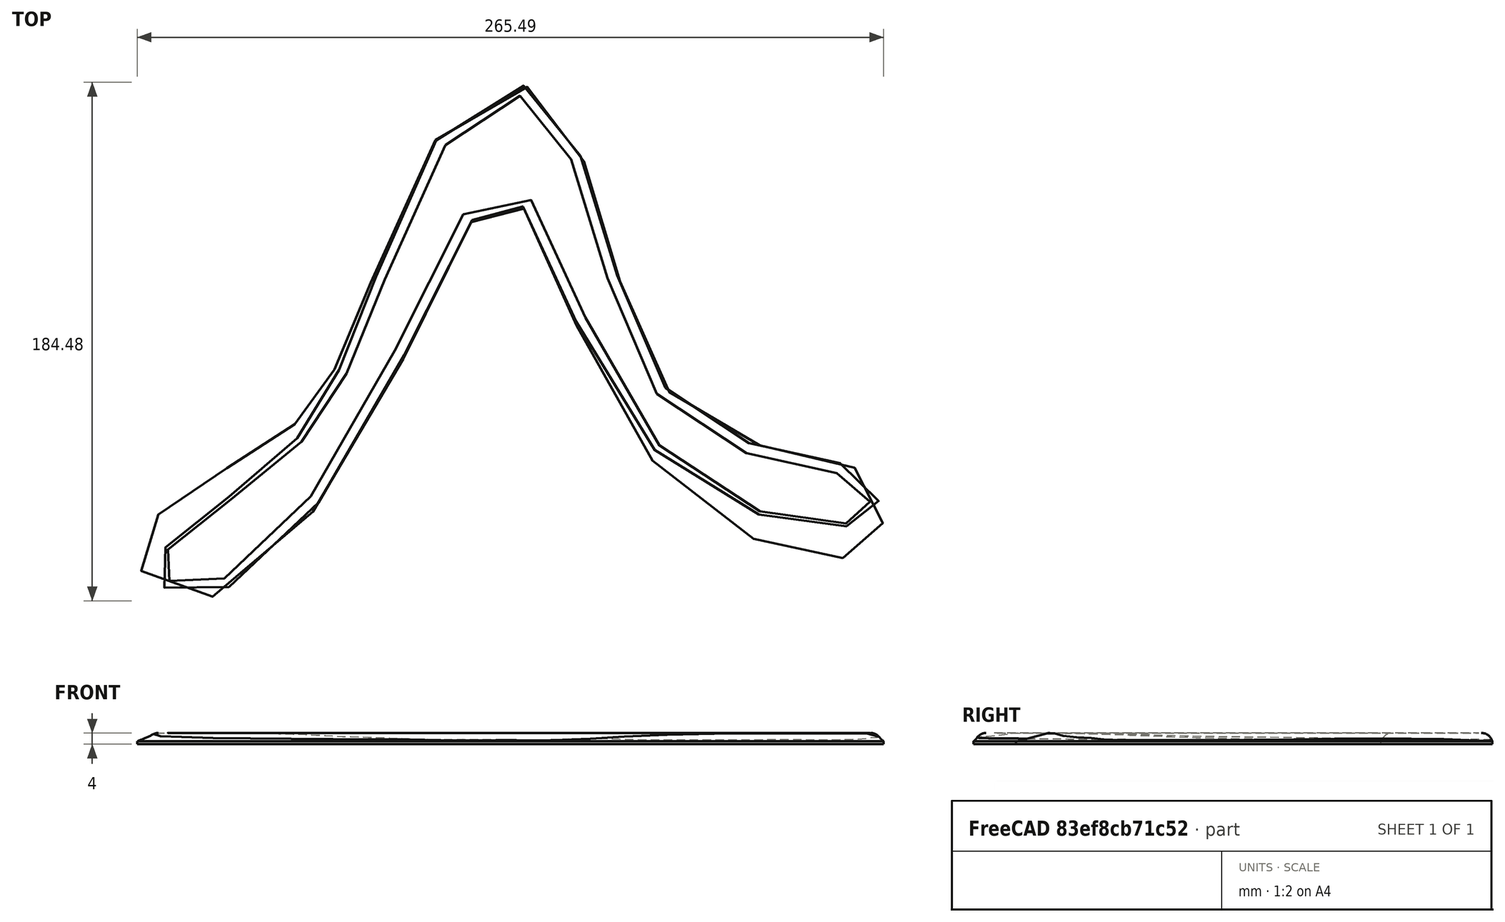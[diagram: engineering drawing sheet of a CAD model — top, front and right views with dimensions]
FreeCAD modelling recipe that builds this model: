
FCSTD DOCUMENT  (FreeCAD 1.2R46491 (Git))
Label: dings
License: All rights reserved
objects: App::Point×2, Sketcher::SketchObject×2, PartDesign::AdditiveLoft×1, PartDesign::Pad×1, PartDesign::Fillet×1, PartDesign::Body×1, App::Part×1
note: 14 computed .brp shape members not serialized (recipe doc carries the construction recipe); baked Part::Feature solids carry a one-line shape summary decoded from their .brp

FEATURE [App::Point] Origin001  label="Origin-Point"
  Role = Origin
FEATURE [App::Point] Origin003  label="Origin-Point001"
  Role = Origin
FEATURE [Sketcher::SketchObject] Sketch  label="Outline"
  ArcFitTolerance = 1e-06
  AttachmentSupport = -> [Origin002]
  ExternalTypes = [0]
  FullyConstrained = false
  MakeInternals = true
  MapMode = 5
  sketch-geometry (29):
    g0: BSplineCurve PolesCount=14 KnotsCount=14 Degree=3 IsPeriodic=1
    g1-g13: GeomPoint [constr] x13 (B-spline internal-alignment scaffolding for g0; pole/knot coordinates omitted)
    g14-g27: Circle [constr] x14 (B-spline internal-alignment scaffolding for g0; pole/knot coordinates omitted)
    g28: GeomPoint [constr] X=-23.3118 Y=8.01846 Z=0
  constraints (29):
    c: InternalAlignment(g1-g14 -> g0) x14
    c: Weight(g14) = 1
    c: InternalAlignment(g15,g0)
    c: Equal(g15,g14)
    c: InternalAlignment(g16,g0)
    c: Equal(g16,g14)
    c: InternalAlignment(g17,g0)
    c: Equal(g17,g14)
    c: InternalAlignment(g18,g0)
    c: Equal(g18,g14)
    c: InternalAlignment(g19,g0)
    c: Equal(g19,g14)
    c: InternalAlignment(g20,g0)
    c: Equal(g20,g14)
    c: InternalAlignment(g21,g0)
    c: Equal(g21,g14)
    c: InternalAlignment(g22,g0)
    c: Equal(g22,g14)
    c: InternalAlignment(g23,g0)
    c: Equal(g23,g14)
    c: InternalAlignment(g24,g0)
    c: Equal(g24,g14)
    c: InternalAlignment(g25,g0)
    c: Equal(g25,g14)
    c: InternalAlignment(g26,g0)
    c: Equal(g26,g14)
    c: InternalAlignment(g27,g0)
    c: Equal(g27,g14)
    c: InternalAlignment(g28,g0)
FEATURE [Sketcher::SketchObject] Sketch001  label="Top Outline"
  ArcFitTolerance = 1e-06
  AttachmentOffset = pos=(0,0,3) rot=(0,0,1;0rad)
  AttachmentSupport = -> [Origin002]
  ExternalTypes = [0]
  FullyConstrained = false
  MakeInternals = true
  MapMode = 5
  Placement = pos=(0,0,3) rot=(0,0,1;0rad)
  sketch-geometry (29):
    g0-g12: GeomPoint [constr] x13 (B-spline internal-alignment scaffolding for g13; pole/knot coordinates omitted)
    g13: BSplineCurve PolesCount=14 KnotsCount=14 Degree=3 IsPeriodic=1
    g14-g27: Circle [constr] x14 (B-spline internal-alignment scaffolding for g13; pole/knot coordinates omitted)
    g28: GeomPoint [constr] X=-22.3923 Y=6.96138 Z=0
  constraints (30):
    c: InternalAlignment(g0-g12 -> g13) x13
    c: InternalAlignment(g14,g13)
    c: Weight(g14) = 1
    c: InternalAlignment(g15,g13)
    c: Equal(g15,g14)
    c: InternalAlignment(g16,g13)
    c: Equal(g16,g14)
    c: InternalAlignment(g17,g13)
    c: Equal(g17,g14)
    c: InternalAlignment(g18,g13)
    c: Equal(g18,g14)
    c: InternalAlignment(g19,g13)
    c: Equal(g19,g14)
    c: InternalAlignment(g20,g13)
    c: Equal(g20,g14)
    c: InternalAlignment(g21,g13)
    c: Equal(g21,g14)
    c: InternalAlignment(g22,g13)
    c: Equal(g22,g14)
    c: InternalAlignment(g23,g13)
    c: Equal(g23,g14)
    c: InternalAlignment(g24,g13)
    c: Equal(g24,g14)
    c: InternalAlignment(g25,g13)
    c: Equal(g25,g14)
    c: InternalAlignment(g26,g13)
    c: Equal(g26,g14)
    c: InternalAlignment(g27,g13)
    c: Equal(g27,g14)
    c: InternalAlignment(g28,g13)
FEATURE [PartDesign::AdditiveLoft] AdditiveLoft  label="Airfoil Loft"
  Closed = false
  Profile = -> Sketch
  Refine = true
  Ruled = false
  Sections = -> [Sketch001]
  Suppressed = false
FEATURE [PartDesign::Pad] Pad  label="Bottom Extrusion"
  BaseFeature = -> AdditiveLoft
  Direction = (0,0,-1)
  Length = 1
  Length2 = 10
  Profile = -> AdditiveLoft [Face1]
  Refine = true
  SideType = 0
  Suppressed = false
  Type = 0
  Type2 = 0
FEATURE [PartDesign::Fillet] Fillet  label="Airfoil Fillet"
  Base = -> Pad [Edge3]
  BaseFeature = -> Pad
  Radius = 4
  Refine = true
  SupportTransform = false
  Suppressed = false
  UseAllEdges = false
FEATURE [PartDesign::Body] Body  label="Boomerang"
  AllowCompound = true
  Group = -> [Sketch,Sketch001,AdditiveLoft,Pad,Fillet]
  Origin = -> Origin002
  Tip = -> Fillet
FEATURE [App::Part] Part
  Group = -> [Body]
  Origin = -> Origin
